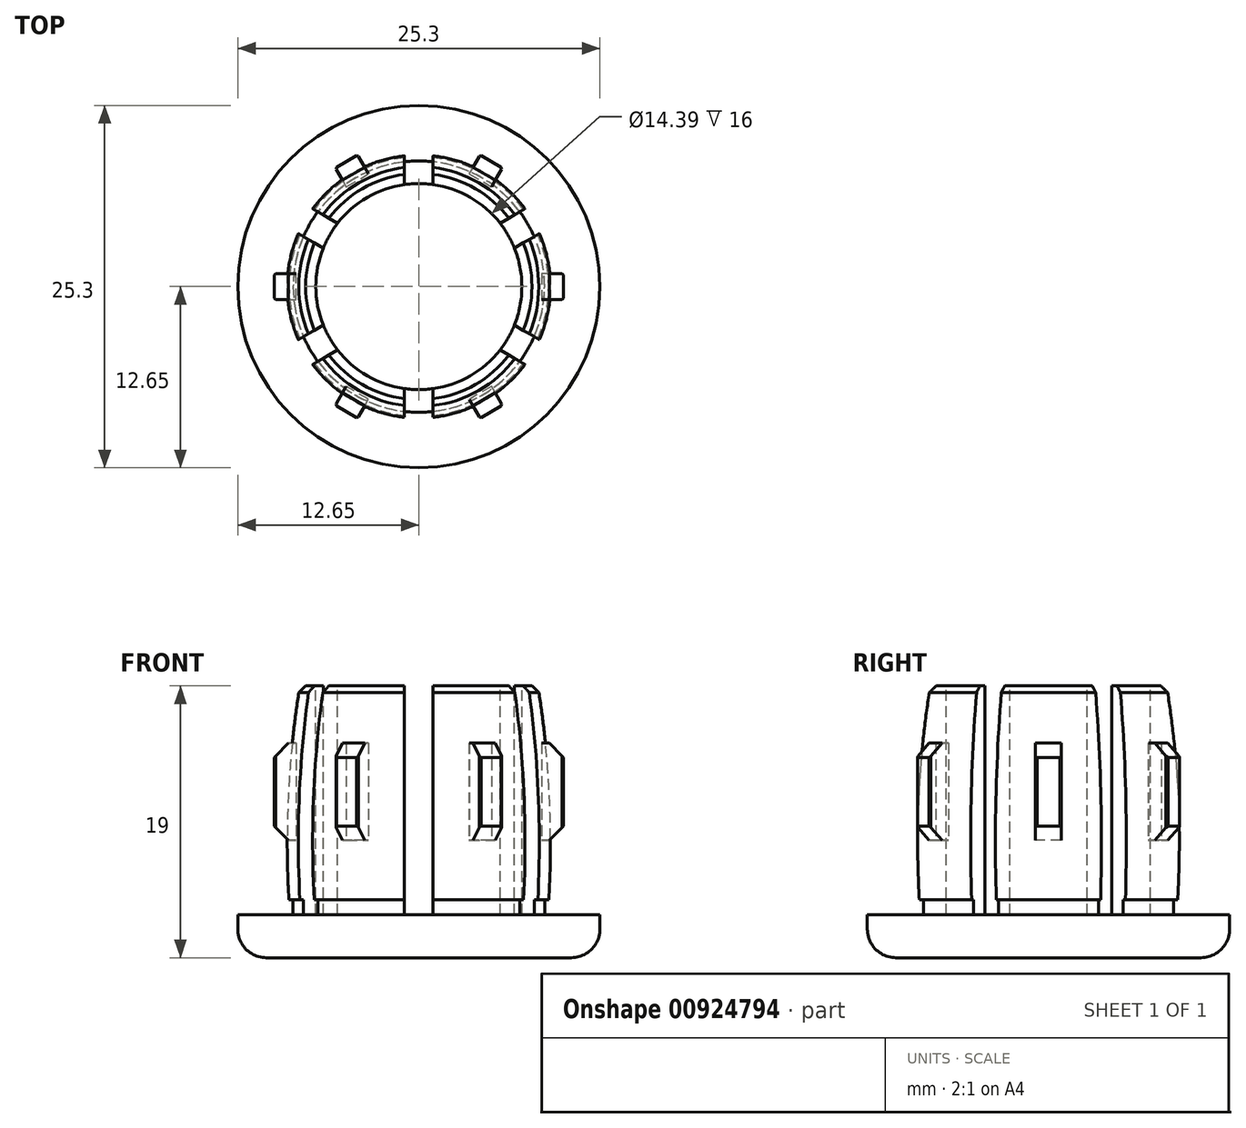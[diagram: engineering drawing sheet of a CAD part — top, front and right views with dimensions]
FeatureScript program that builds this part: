
annotation { "Feature Type Name" : "Feature", "Feature Type Description" : "" }
export const myFeature = defineFeature(function(context is Context, id is Id, definition is map)
    precondition{}
    {
        {
            var Q0;
            Q0=qCreatedBy(makeId("Top.planeOp"),FACE);
            var sketch = newSketch(context, id + "F0", { "sketchPlane" : qUnion([Q0])});
            skLineSegment(sketch, "E0", {"start": v(-20.13, 0) * mm, "end": v(17.3, 0) * mm, "construction": true});
            skLineSegment(sketch, "E1", {"start": v(0, 15.73) * mm, "end": v(0, -12.65) * mm, "construction": true});
            skCircle(sketch, "E2", {"center": v(0, 0) * mm, "radius": 12.65 * mm});
            skCircle(sketch, "E3", {"center": v(0, 0) * mm, "radius": 8.7 * mm});
            skSolve(sketch);
        }
        {
            var Q0;
            Q0 = qSketchRegion(id + "F0", true);
            var Q1;
            Q1=makeQuery(id+"F0.imprint","IMPRINT",FACE,{"disambiguationData":[TD([[makeQuery(id+"F0.imprint","IMPRINT",EDGE,{"derivedFrom":sQuery(id+"F0.wireOp",EDGE,"E3")}),1.0]])]});
            extrude(context, id + "F1", {"entities" : qUnion([Q0, Q1]), "depth" : 3 * mm, "offsetDistance" : 25 * mm});
        }
        {
            var Q0;
            Q0=qCreatedBy(makeId("Front.planeOp"),FACE);
            var sketch = newSketch(context, id + "F2", { "sketchPlane" : qUnion([Q0])});
            skLineSegment(sketch, "E4", {"start": v(0, 28.56) * mm, "end": v(0, 19) * mm, "construction": true});
            skLineSegment(sketch, "E5", {"start": v(-21.46, 24.49) * mm, "end": v(18.54, 24.49) * mm, "construction": true});
            skLineSegment(sketch, "E6", {"start": v(18.54, 24.49) * mm, "end": v(18.54, 24.17) * mm, "construction": true});
            skLineSegment(sketch, "E7", {"start": v(9.02, 28.56) * mm, "end": v(9.02, 4.04) * mm, "construction": true});
            skLineSegment(sketch, "E8", {"start": v(7.2, 3) * mm, "end": v(8.78, 3) * mm});
            skLineSegment(sketch, "E9", {"start": v(7.2, 19) * mm, "end": v(7.9, 19) * mm});
            skLineSegment(sketch, "E10", {"start": v(7.9, 19) * mm, "end": v(8.38, 18.54) * mm});
            skArc(sketch, "E11", {"start": v(9.07, 4.04) * mm, "mid": v(9.12, 11.3) * mm, "end": v(8.38, 18.54) * mm});
            skLineSegment(sketch, "E12", {"start": v(9.07, 4.04) * mm, "end": v(8.78, 4.04) * mm});
            skLineSegment(sketch, "E13", {"start": v(8.78, 4.04) * mm, "end": v(8.78, 3) * mm});
            skPoint(sketch, "E14.orphan", {"position": v(9, 3) * mm});
            skLineSegment(sketch, "E15", {"start": v(7.2, 19) * mm, "end": v(7.2, 3) * mm});
            skLineSegment(sketch, "E16.trimOffspring", {"start": v(0, 3) * mm, "end": v(0, -7.9) * mm, "construction": true});
            skSolve(sketch);
        }
        {
            var Q0;
            Q0=makeQuery(id+"F1.opExtrude","CAP_EDGE",EDGE,{"disambiguationData":[OSD([sQuery(id+"F0.wireOp",EDGE,"E2")])],"isStart":true});
            fillet(context, id + "F3", {"entities" : qUnion([Q0]), "radius" : 2 * mm, "tangentPropagation" : true, "allowEdgeOverflow" : false});
        }
        {
            var Q0;
            Q0 = qSketchRegion(id + "F2", true);
            var Q1;
            Q1=sQuery(id+"F2.wireOp",EDGE,"E4");
            revolve(context, id + "F4", {"operationType" : NewBodyOperationType.ADD, "surfaceOperationType" : NewSurfaceOperationType.NEW, "entities" : qUnion([Q0]), "axis" : qUnion([Q1]), "revolveType" : RevolveType.FULL});
        }
        {
            var Q0;
            Q0=qCreatedBy(makeId("Front.planeOp"),FACE);
            var sketch = newSketch(context, id + "F5", { "sketchPlane" : qUnion([Q0])});
            skLineSegment(sketch, "E17", {"start": v(0, 40.53) * mm, "end": v(0, -4.6) * mm, "construction": true});
            skLineSegment(sketch, "E18", {"start": v(-18.53, 3.02) * mm, "end": v(25.87, 3.02) * mm, "construction": true});
            skLineSegment(sketch, "E19.bottom", {"start": v(-1, 31.73) * mm, "end": v(1, 31.73) * mm});
            skLineSegment(sketch, "E19.top", {"start": v(-1, 3.02) * mm, "end": v(1, 3.02) * mm});
            skLineSegment(sketch, "E19.left", {"start": v(-1, 31.73) * mm, "end": v(-1, 3.02) * mm});
            skLineSegment(sketch, "E19.right", {"start": v(1, 31.73) * mm, "end": v(1, 3.02) * mm});
            skSolve(sketch);
        }
        {
            var Q0;
            Q0 = qSketchRegion(id + "F5", true);
            extrude(context, id + "F6", {"entities" : qUnion([Q0]), "depth" : 14 * mm, "offsetDistance" : 25 * mm});
        }
        {
            var Q0;
            Q0=makeQuery(id+"F6.opExtrude","SWEPT_BODY",BODY,{"disambiguationData":[OSD([sQuery(id+"F5.wireOp",EDGE,"E19.bottom"),sQuery(id+"F5.wireOp",EDGE,"E19.top"),sQuery(id+"F5.wireOp",EDGE,"E19.left"),sQuery(id+"F5.wireOp",EDGE,"E19.right")])]});
            var Q1;
            Q1=sQuery(id+"F0.wireOp",EDGE,"E3");
            circularPattern(context, id + "F7", {"operationType" : NewBodyOperationType.REMOVE, "entities" : qUnion([Q0]), "axis" : qUnion([Q1]), "angle" : 360 * degree, "instanceCount" : 6, "equalSpace" : true});
        }
        {
            var Q0;
            {var subQ0=sQuery(id+"F0.wireOp",EDGE,"E2");Q0=makeQuery(id+"F4.boolean.opBoolean","SPLIT",FACE,{"disambiguationData":[TD([makeQuery(id+"F1.opExtrude","SWEPT_FACE",FACE,{"disambiguationData":[OSD([subQ0])]})])],"derivedFrom":makeQuery(id+"F1.opExtrude","CAP_FACE",FACE,{"disambiguationData":[OSD([subQ0])],"isStart":false})});}
            cPlane(context, id + "F8", {"entities" : qUnion([Q0]), "cplaneType" : CPlaneType.OFFSET, "offset" : 2 * mm, "width" : 150 * mm, "height" : 150 * mm});
        }
        {
            var Q0;
            Q0=qCreatedBy(id+"F8.planeOp",FACE);
            var sketch = newSketch(context, id + "F9", { "sketchPlane" : qUnion([Q0])});
            skLineSegment(sketch, "E20", {"start": v(-8.58, 0.9) * mm, "end": v(-10.1, 0.9) * mm});
            skLineSegment(sketch, "E21", {"start": v(-10.1, 0.9) * mm, "end": v(-10.1, -0.9) * mm});
            skLineSegment(sketch, "E22", {"start": v(-10.1, -0.9) * mm, "end": v(-8.57, -0.9) * mm});
            skLineSegment(sketch, "E23", {"start": v(-8.57, -0.9) * mm, "end": v(-8.58, 0.9) * mm});
            skSolve(sketch);
        }
        {
            var Q0;
            Q0 = qSketchRegion(id + "F9", true);
            extrude(context, id + "F10", {"entities" : qUnion([Q0]), "depth" : 10 * mm, "offsetDistance" : 25 * mm, "hasSecondDirection" : true, "secondDirectionOppositeDirection" : false, "secondDirectionDepth" : 3.2 * mm});
        }
        {
            var Q0;
            Q0=makeQuery(id+"F10.opExtrude","SWEPT_EDGE",EDGE,{"disambiguationData":[OSD([sQuery(id+"F9.wireOp",EDGE,"E21"),sQuery(id+"F9.wireOp",EDGE,"E22")])]});
            var Q1;
            Q1=makeQuery(id+"F10.opExtrude","SWEPT_EDGE",EDGE,{"disambiguationData":[OSD([sQuery(id+"F9.wireOp",EDGE,"E20"),sQuery(id+"F9.wireOp",EDGE,"E21")])]});
            chamfer(context, id + "F11", {"entities" : qUnion([Q0, Q1]), "width" : .1 * mm, "tangentPropagation" : true});
        }
        {
            var Q0;
            Q0=makeQuery(id+"F10.opExtrude","SWEPT_BODY",BODY,{"disambiguationData":[OSD([sQuery(id+"F9.wireOp",EDGE,"E20"),sQuery(id+"F9.wireOp",EDGE,"E21"),sQuery(id+"F9.wireOp",EDGE,"E22"),sQuery(id+"F9.wireOp",EDGE,"E23")])]});
            var Q1;
            Q1=makeQuery(id+"F1.opExtrude","SWEPT_BODY",BODY,{"disambiguationData":[OSD([sQuery(id+"F0.wireOp",EDGE,"E2")])]});
            var Q2;
            Q2=sQuery(id+"F0.wireOp",EDGE,"E3");
            circularPattern(context, id + "F12", {"entities" : qUnion([Q0, Q1]), "axis" : qUnion([Q2]), "angle" : 360 * degree, "instanceCount" : 6, "equalSpace" : true});
        }
        {
            var Q0;
            Q0=makeQuery(id+"F12.opPattern","COPY",EDGE,{"derivedFrom":makeQuery(id+"F10.opExtrude","CAP_EDGE",EDGE,{"disambiguationData":[OSD([sQuery(id+"F9.wireOp",EDGE,"E21")])],"isStart":false}),"instanceName":"1"});
            var Q1;
            Q1=makeQuery(id+"F12.opPattern","COPY",EDGE,{"derivedFrom":makeQuery(id+"F10.opExtrude","CAP_EDGE",EDGE,{"disambiguationData":[OSD([sQuery(id+"F9.wireOp",EDGE,"E21")])],"isStart":false}),"instanceName":"2"});
            var Q2;
            Q2=makeQuery(id+"F12.opPattern","COPY",EDGE,{"derivedFrom":makeQuery(id+"F10.opExtrude","CAP_EDGE",EDGE,{"disambiguationData":[OSD([sQuery(id+"F9.wireOp",EDGE,"E21")])],"isStart":false}),"instanceName":"3"});
            var Q3;
            Q3=makeQuery(id+"F12.opPattern","COPY",EDGE,{"derivedFrom":makeQuery(id+"F10.opExtrude","CAP_EDGE",EDGE,{"disambiguationData":[OSD([sQuery(id+"F9.wireOp",EDGE,"E21")])],"isStart":false}),"instanceName":"4"});
            var Q4;
            Q4=makeQuery(id+"F12.opPattern","COPY",EDGE,{"derivedFrom":makeQuery(id+"F10.opExtrude","CAP_EDGE",EDGE,{"disambiguationData":[OSD([sQuery(id+"F9.wireOp",EDGE,"E21")])],"isStart":false}),"instanceName":"5"});
            var Q5;
            Q5=makeQuery(id+"F12.opPattern","COPY",EDGE,{"derivedFrom":makeQuery(id+"F10.opExtrude","CAP_EDGE",EDGE,{"disambiguationData":[OSD([sQuery(id+"F9.wireOp",EDGE,"E21")])],"isStart":true}),"instanceName":"5"});
            var Q6;
            Q6=makeQuery(id+"F12.opPattern","COPY",EDGE,{"derivedFrom":makeQuery(id+"F10.opExtrude","CAP_EDGE",EDGE,{"disambiguationData":[OSD([sQuery(id+"F9.wireOp",EDGE,"E21")])],"isStart":true}),"instanceName":"4"});
            var Q7;
            Q7=makeQuery(id+"F10.opExtrude","CAP_EDGE",EDGE,{"disambiguationData":[OSD([sQuery(id+"F9.wireOp",EDGE,"E21")])],"isStart":true});
            var Q8;
            Q8=makeQuery(id+"F10.opExtrude","CAP_EDGE",EDGE,{"disambiguationData":[OSD([sQuery(id+"F9.wireOp",EDGE,"E21")])],"isStart":false});
            var Q9;
            Q9=makeQuery(id+"F12.opPattern","COPY",EDGE,{"derivedFrom":makeQuery(id+"F10.opExtrude","CAP_EDGE",EDGE,{"disambiguationData":[OSD([sQuery(id+"F9.wireOp",EDGE,"E21")])],"isStart":true}),"instanceName":"1"});
            var Q10;
            Q10=makeQuery(id+"F12.opPattern","COPY",EDGE,{"derivedFrom":makeQuery(id+"F10.opExtrude","CAP_EDGE",EDGE,{"disambiguationData":[OSD([sQuery(id+"F9.wireOp",EDGE,"E21")])],"isStart":true}),"instanceName":"2"});
            var Q11;
            Q11=makeQuery(id+"F12.opPattern","COPY",EDGE,{"derivedFrom":makeQuery(id+"F10.opExtrude","CAP_EDGE",EDGE,{"disambiguationData":[OSD([sQuery(id+"F9.wireOp",EDGE,"E21")])],"isStart":true}),"instanceName":"3"});
            chamfer(context, id + "F13", {"entities" : qUnion([Q0, Q1, Q2, Q3, Q4, Q5, Q6, Q7, Q8, Q9, Q10, Q11]), "width" : 1 * mm, "tangentPropagation" : true});
        }
    });
